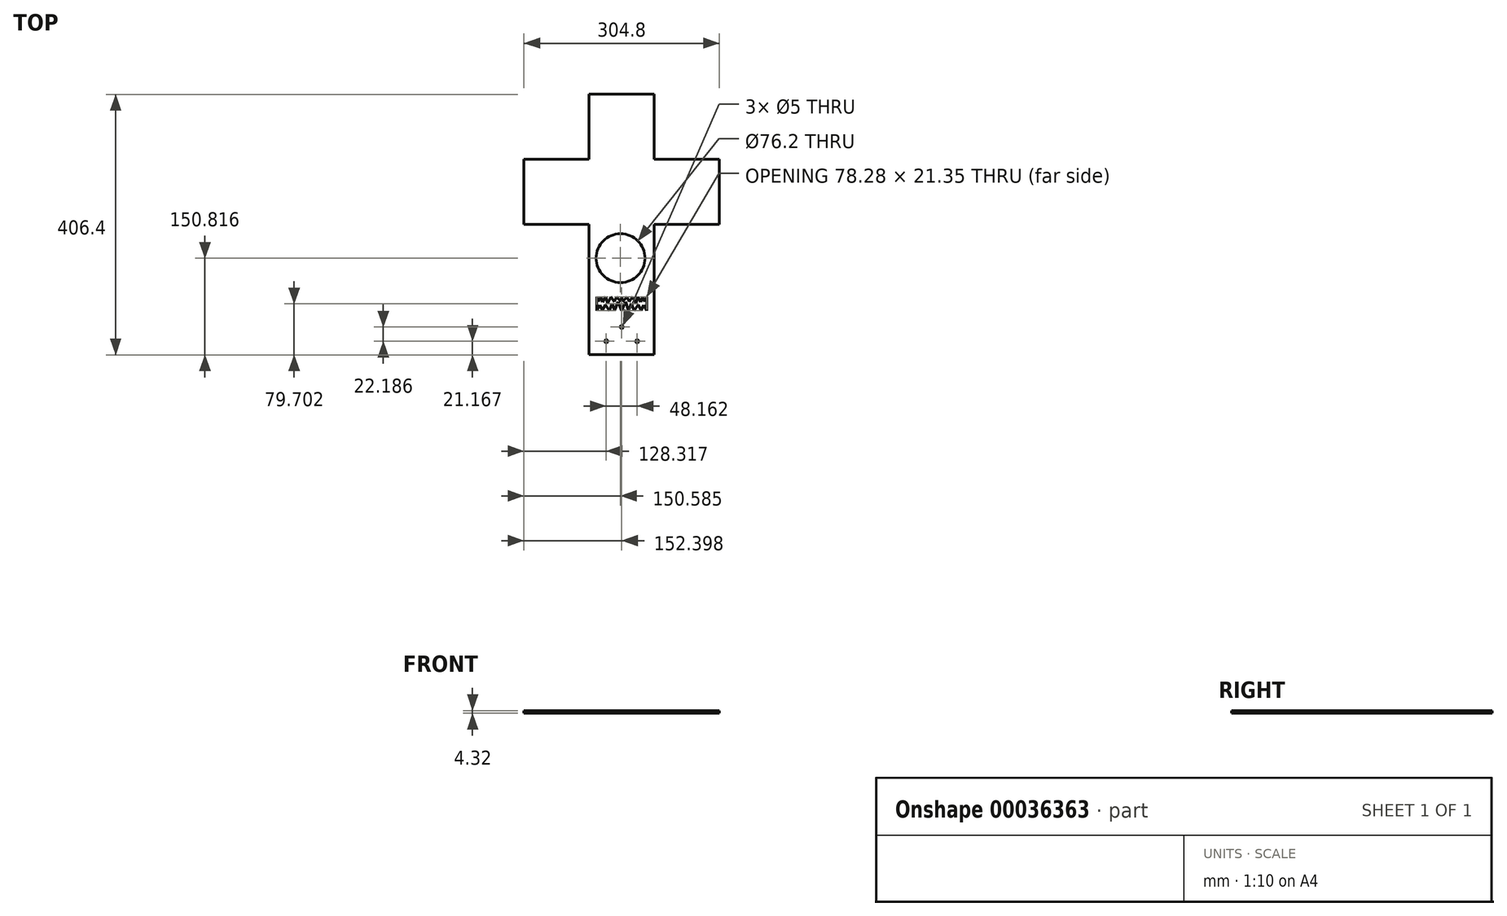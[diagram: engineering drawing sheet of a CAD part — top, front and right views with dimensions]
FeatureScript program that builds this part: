
annotation { "Feature Type Name" : "Feature", "Feature Type Description" : "" }
export const myFeature = defineFeature(function(context is Context, id is Id, definition is map)
    precondition{}
    {
        {
            var Q0;
            Q0=qCreatedBy(makeId("Top.planeOp"),FACE);
            var sketch = newSketch(context, id + "F0", { "sketchPlane" : qUnion([Q0])});
            skLineSegment(sketch, "E0.bottom", {"start": v(-53.22, 127.85) * mm, "end": v(48.38, 127.85) * mm});
            skLineSegment(sketch, "E0.top", {"start": v(-53.22, 26.25) * mm, "end": v(48.38, 26.25) * mm});
            skLineSegment(sketch, "E0.left", {"start": v(-53.22, 127.85) * mm, "end": v(-53.22, 26.25) * mm});
            skLineSegment(sketch, "E0.right", {"start": v(48.38, 127.85) * mm, "end": v(48.38, 26.25) * mm});
            skLineSegment(sketch, "E1.MirrorCS", {"start": v(-53.22, -75.35) * mm, "end": v(-53.22, 26.25) * mm});
            skLineSegment(sketch, "E2.MirrorCS", {"start": v(-53.22, -75.35) * mm, "end": v(48.38, -75.35) * mm});
            skLineSegment(sketch, "E3.MirrorCS", {"start": v(48.38, -75.35) * mm, "end": v(48.38, 26.25) * mm});
            skLineSegment(sketch, "E4.MirrorCS", {"start": v(-53.22, -75.35) * mm, "end": v(-154.82, -75.35) * mm});
            skLineSegment(sketch, "E5.MirrorCS", {"start": v(-154.82, -75.35) * mm, "end": v(-154.82, 26.25) * mm});
            skLineSegment(sketch, "E6.MirrorCS", {"start": v(-53.22, 26.25) * mm, "end": v(-154.82, 26.25) * mm});
            skLineSegment(sketch, "E7.MirrorCS", {"start": v(149.98, 26.25) * mm, "end": v(48.38, 26.25) * mm});
            skLineSegment(sketch, "E8.MirrorCS", {"start": v(149.98, -75.35) * mm, "end": v(149.98, 26.25) * mm});
            skLineSegment(sketch, "E9.MirrorCS", {"start": v(149.98, -75.35) * mm, "end": v(48.38, -75.35) * mm});
            skLineSegment(sketch, "E10.MirrorCS", {"start": v(-53.22, -75.35) * mm, "end": v(-53.22, -176.95) * mm});
            skLineSegment(sketch, "E11.MirrorCS", {"start": v(-53.22, -176.95) * mm, "end": v(48.38, -176.95) * mm});
            skLineSegment(sketch, "E12.MirrorCS", {"start": v(48.38, -75.35) * mm, "end": v(48.38, -176.95) * mm});
            skLineSegment(sketch, "E13.MirrorCS", {"start": v(-53.22, -278.55) * mm, "end": v(-53.22, -176.95) * mm});
            skLineSegment(sketch, "E14.MirrorCS", {"start": v(-53.22, -278.55) * mm, "end": v(48.38, -278.55) * mm});
            skLineSegment(sketch, "E15.MirrorCS", {"start": v(48.38, -278.55) * mm, "end": v(48.38, -176.95) * mm});
            skCircle(sketch, "E16", {"center": v(-26.5, -257.38) * mm, "radius": 2.5 * mm});
            skCircle(sketch, "E17.MirrorC", {"center": v(21.66, -257.38) * mm, "radius": 2.5 * mm});
            skLineSegment(sketch, "E18.left", {"start": v(-41.56, -188.17) * mm, "end": v(-41.56, -209.52) * mm});
            skLineSegment(sketch, "E19.MirrorCS", {"start": v(36.72, -188.17) * mm, "end": v(36.72, -209.52) * mm});
            skCircle(sketch, "E20", {"center": v(-2.42, -235.2) * mm, "radius": 2.5 * mm});
            skCircle(sketch, "E21", {"center": v(-4.23, -127.73) * mm, "radius": 38.1 * mm});
            skLineSegment(sketch, "E22", {"start": v(-41.56, -209.52) * mm, "end": v(-36.52, -200.75) * mm});
            skLineSegment(sketch, "E23", {"start": v(-36.52, -200.75) * mm, "end": v(-32.67, -209.52) * mm});
            skLineSegment(sketch, "E24", {"start": v(-32.67, -209.52) * mm, "end": v(-28.26, -199.97) * mm});
            skLineSegment(sketch, "E25", {"start": v(-28.26, -199.97) * mm, "end": v(-22, -209.52) * mm});
            skLineSegment(sketch, "E26", {"start": v(-22, -209.52) * mm, "end": v(-17.47, -198.06) * mm});
            skLineSegment(sketch, "E27", {"start": v(-17.47, -198.06) * mm, "end": v(-13.24, -209.52) * mm});
            skLineSegment(sketch, "E28", {"start": v(-13.24, -209.52) * mm, "end": v(-8.46, -195.87) * mm});
            skLineSegment(sketch, "E29", {"start": v(-8.46, -195.87) * mm, "end": v(-2.42, -209.52) * mm});
            skLineSegment(sketch, "E30.MirrorCS", {"start": v(3.62, -195.87) * mm, "end": v(-2.42, -209.52) * mm});
            skLineSegment(sketch, "E31.MirrorCS", {"start": v(8.4, -209.52) * mm, "end": v(3.62, -195.87) * mm});
            skLineSegment(sketch, "E32.MirrorCS", {"start": v(12.63, -198.06) * mm, "end": v(8.4, -209.52) * mm});
            skLineSegment(sketch, "E33.MirrorCS", {"start": v(17.15, -209.52) * mm, "end": v(12.63, -198.06) * mm});
            skLineSegment(sketch, "E34.MirrorCS", {"start": v(23.41, -199.97) * mm, "end": v(17.15, -209.52) * mm});
            skLineSegment(sketch, "E35.MirrorCS", {"start": v(27.83, -209.52) * mm, "end": v(23.41, -199.97) * mm});
            skLineSegment(sketch, "E36.MirrorCS", {"start": v(31.68, -200.75) * mm, "end": v(27.83, -209.52) * mm});
            skLineSegment(sketch, "E37.MirrorCS", {"start": v(36.72, -209.52) * mm, "end": v(31.68, -200.75) * mm});
            skLineSegment(sketch, "E38", {"start": v(-41.56, -188.17) * mm, "end": v(-38.59, -195.75) * mm});
            skLineSegment(sketch, "E39", {"start": v(-38.59, -195.75) * mm, "end": v(-35.36, -188.17) * mm});
            skLineSegment(sketch, "E40", {"start": v(-35.36, -188.17) * mm, "end": v(-32.32, -196.26) * mm});
            skLineSegment(sketch, "E41", {"start": v(-32.32, -196.26) * mm, "end": v(-27.63, -188.17) * mm});
            skLineSegment(sketch, "E42", {"start": v(-27.63, -188.17) * mm, "end": v(-24.2, -198) * mm});
            skLineSegment(sketch, "E43", {"start": v(-24.2, -198) * mm, "end": v(-19.15, -188.17) * mm});
            skLineSegment(sketch, "E44", {"start": v(-19.15, -188.17) * mm, "end": v(-14.32, -195.87) * mm});
            skLineSegment(sketch, "E45", {"start": v(-14.32, -195.87) * mm, "end": v(-10.35, -188.17) * mm});
            skLineSegment(sketch, "E46", {"start": v(-10.35, -188.17) * mm, "end": v(-4, -195.87) * mm});
            skLineSegment(sketch, "E47", {"start": v(-4, -195.87) * mm, "end": v(-2.42, -188.17) * mm});
            skLineSegment(sketch, "E48.MirrorCS", {"start": v(5.5, -188.17) * mm, "end": v(-0.85, -195.87) * mm});
            skLineSegment(sketch, "E49.MirrorCS", {"start": v(-0.85, -195.87) * mm, "end": v(-2.42, -188.17) * mm});
            skLineSegment(sketch, "E50.MirrorCS", {"start": v(9.47, -195.87) * mm, "end": v(5.5, -188.17) * mm});
            skLineSegment(sketch, "E51.MirrorCS", {"start": v(14.3, -188.17) * mm, "end": v(9.47, -195.87) * mm});
            skLineSegment(sketch, "E52.MirrorCS", {"start": v(19.35, -198) * mm, "end": v(14.3, -188.17) * mm});
            skLineSegment(sketch, "E53.MirrorCS", {"start": v(22.79, -188.17) * mm, "end": v(19.35, -198) * mm});
            skLineSegment(sketch, "E54.MirrorCS", {"start": v(27.48, -196.26) * mm, "end": v(22.79, -188.17) * mm});
            skLineSegment(sketch, "E55.MirrorCS", {"start": v(30.52, -188.17) * mm, "end": v(27.48, -196.26) * mm});
            skLineSegment(sketch, "E56.MirrorCS", {"start": v(33.74, -195.75) * mm, "end": v(30.52, -188.17) * mm});
            skLineSegment(sketch, "E57.MirrorCS", {"start": v(36.72, -188.17) * mm, "end": v(33.74, -195.75) * mm});
            skSolve(sketch);
        }
        {
            var Q0;
            Q0=makeQuery(id+"F0.imprint","IMPRINT",FACE,{"disambiguationData":[TD([[makeQuery(id+"F0.imprint","IMPRINT",EDGE,{"derivedFrom":sQuery(id+"F0.wireOp",EDGE,"E1.MirrorCS")}),1.0]])]});
            var Q1;
            Q1=makeQuery(id+"F0.imprint","IMPRINT",FACE,{"disambiguationData":[TD([[makeQuery(id+"F0.imprint","IMPRINT",EDGE,{"derivedFrom":sQuery(id+"F0.wireOp",EDGE,"E0.top")}),-1.0]])]});
            var Q2;
            Q2=makeQuery(id+"F0.imprint","IMPRINT",FACE,{"disambiguationData":[TD([[makeQuery(id+"F0.imprint","IMPRINT",EDGE,{"derivedFrom":sQuery(id+"F0.wireOp",EDGE,"E0.bottom")}),-1.0]])]});
            var Q3;
            Q3=makeQuery(id+"F0.imprint","IMPRINT",FACE,{"disambiguationData":[TD([[makeQuery(id+"F0.imprint","IMPRINT",EDGE,{"derivedFrom":sQuery(id+"F0.wireOp",EDGE,"E3.MirrorCS")}),-1.0]])]});
            var Q4;
            Q4=makeQuery(id+"F0.imprint","IMPRINT",FACE,{"disambiguationData":[TD([[makeQuery(id+"F0.imprint","IMPRINT",EDGE,{"derivedFrom":sQuery(id+"F0.wireOp",EDGE,"E2.MirrorCS")}),-1.0]])]});
            var Q5;
            Q5=makeQuery(id+"F0.imprint","IMPRINT",FACE,{"disambiguationData":[TD([[makeQuery(id+"F0.imprint","IMPRINT",EDGE,{"derivedFrom":sQuery(id+"F0.wireOp",EDGE,"E11.MirrorCS")}),-1.0]])]});
            extrude(context, id + "F1", {"entities" : qUnion([Q0, Q1, Q2, Q3, Q4, Q5]), "depth" : 4.32 * mm});
        }
        {
            var Q0;
            Q0 = qSketchRegion(id + "F0", true);
            extrude(context, id + "F2", {"entities" : qUnion([Q0]), "operationType" : NewBodyOperationType.ADD, "depth" : 4.32 * mm});
        }
    });
